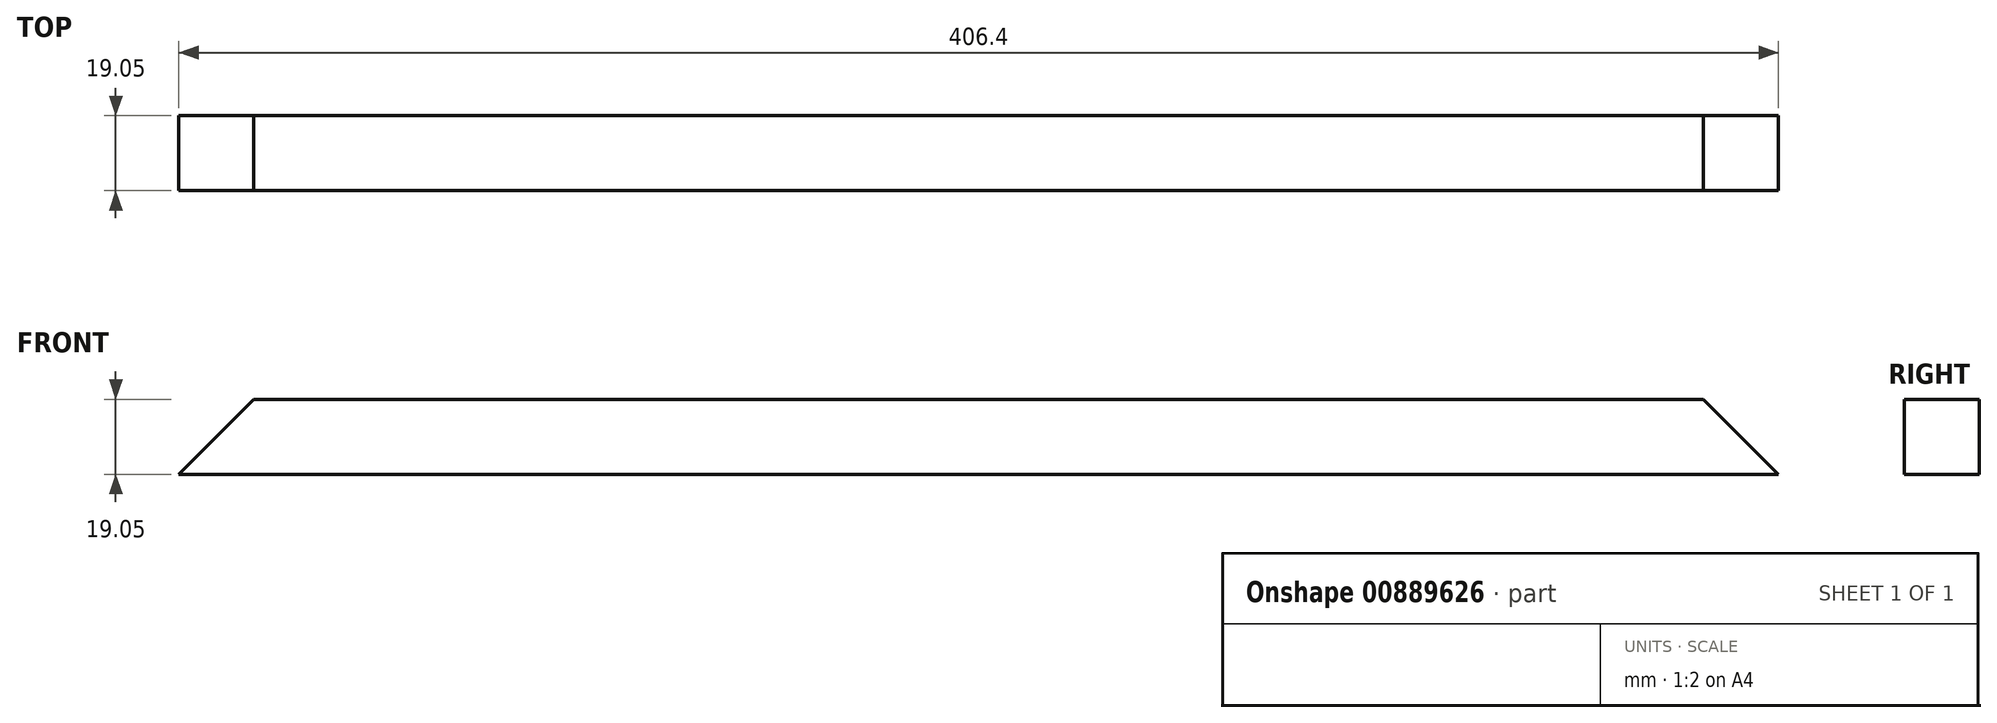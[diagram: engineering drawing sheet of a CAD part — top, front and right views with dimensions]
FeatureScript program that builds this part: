
annotation { "Feature Type Name" : "Feature", "Feature Type Description" : "" }
export const myFeature = defineFeature(function(context is Context, id is Id, definition is map)
    precondition{}
    {
        {
            var Q0;
            Q0=qCreatedBy(makeId("Right.planeOp"),FACE);
            var sketch = newSketch(context, id + "F0", { "sketchPlane" : qUnion([Q0])});
            skLineSegment(sketch, "E0.bottom", {"start": v(0, 0) * mm, "end": v(19.05, 0) * mm});
            skLineSegment(sketch, "E0.top", {"start": v(0, 19.05) * mm, "end": v(19.05, 19.05) * mm});
            skLineSegment(sketch, "E0.left", {"start": v(0, 0) * mm, "end": v(0, 19.05) * mm});
            skLineSegment(sketch, "E0.right", {"start": v(19.05, 0) * mm, "end": v(19.05, 19.05) * mm});
            skSolve(sketch);
        }
        {
            var Q0;
            Q0 = qSketchRegion(id + "F0", true);
            extrude(context, id + "F1", {"entities" : qUnion([Q0]), "depth" : 406.4 * mm, "offsetDistance" : 25.4 * mm});
        }
        {
            var Q0;
            Q0=makeQuery(id+"F1.opExtrude","SWEPT_FACE",FACE,{"disambiguationData":[OSD([sQuery(id+"F0.wireOp",EDGE,"E0.left")])]});
            var sketch = newSketch(context, id + "F2", { "sketchPlane" : qUnion([Q0])});
            skLineSegment(sketch, "E1", {"start": v(0, 0) * mm, "end": v(19.05, 19.05) * mm});
            skLineSegment(sketch, "E2", {"start": v(19.05, 19.05) * mm, "end": v(0, 19.05) * mm});
            skLineSegment(sketch, "E3", {"start": v(0, 19.05) * mm, "end": v(0, 0) * mm});
            skLineSegment(sketch, "E4", {"start": v(406.4, 0) * mm, "end": v(406.4, 19.05) * mm});
            skLineSegment(sketch, "E5", {"start": v(406.4, 19.05) * mm, "end": v(387.35, 19.05) * mm});
            skLineSegment(sketch, "E6", {"start": v(387.35, 19.05) * mm, "end": v(406.4, 0) * mm});
            skSolve(sketch);
        }
        {
            var Q0;
            Q0 = qSketchRegion(id + "F2", true);
            extrude(context, id + "F3", {"entities" : qUnion([Q0]), "operationType" : NewBodyOperationType.REMOVE, "oppositeDirection" : true, "depth" : 19.05 * mm, "offsetDistance" : 25.4 * mm});
        }
    });
